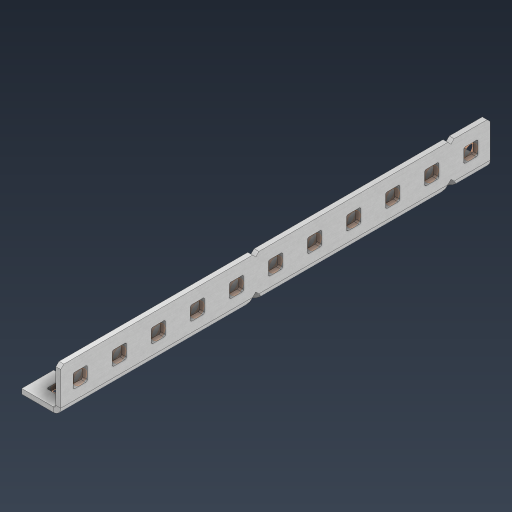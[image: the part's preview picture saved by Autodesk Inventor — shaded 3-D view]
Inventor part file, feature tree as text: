
AUTODESK INVENTOR PART (.ipt)
format: ipt  version: 2024.3 (Build 283343000, 343)  size: 625,664 bytes
history: native  units: in
note: dims shown in document units (in); Inventor stores cm internally (conversion verified against a paired STEP export)
features: other x40, extrude x31, sheet_metal_op x11, pattern_linear x2, mirror x1, chamfer x1, sketch x1
ambient origin geometry x8: Origin, YZ Plane, XZ Plane, XY Plane, X Axis, Y Axis, Z Axis, Center Point
bodies: Solid1 (feature_tree), Body (feature_tree)
feature tree (87):
  sheet_metal_op  "Flanges"
  other  "Flange Pattern Plane"
  other  "Flange Pattern Sketch"
  sheet_metal_op  "Flange Pattern"
  sheet_metal_op  "Body Pattern"
  pattern_linear  "Center Pattern"  Spacing1=5.5in  [1 undecoded]
  other  "Arc Length"
  mirror  "Notch Mirror"
  pattern_linear  "Notch Pattern"  Spacing1=0.0625in  [1 undecoded]
  chamfer  "End Chamfer"
  extrude  "Half Cut"  Depth=0.0625in
  other  "Plate1"
  sketch  "Sketch2"  dims[d0=1.0in d1=5.5in d2=0.0625in d3=0.0625in d4=0.0312in d5=0.125in d6=0.0625in d7=0.5in d8=90.0deg d9=0.0312in d10=0.25in d11=0.0625in d12=0.0625in d16=0.182in d17=0.02in d18=0.0625in d19=0.0in d20=0.25in d21=0.25in d38=4.3307in d40=0.5in d41=0.3937in d43=1.0in d46=0.172in d47=1.0in d48=0.0in d49=0.182in d50=0.02in d51=0.25in d52=0.25in d53=0.0625in d54=0.0in d55=0.172in d56=1.0in d57=0.0in d58=0.25in d60=4.3307in d62=0.5in d63=0.3937in d65=0.5in d85=0.1473in d86=0.1782in d88=0.04in d89=0.0625in d90=0.0in d91=0.04in d92=0.0491in d95=2.5in d96=0.04in d97=0.25in d98=45.0deg d99=0.25in d100=0.5in d101=0.0in d102=2.497in d106=0.182in d107=0.02in d108=0.5in d109=0.5in d110=0.0625in d111=0.0in d112=0.172in d113=0.5in d114=0.0in d117=0.5in d118=0.5in d119=0.5in]
  other  "Plate2"
  sheet_metal_op  "Bend1"
  sheet_metal_op  "Corner1"
  other  "Srf1"
  other  "Srf2"
  other  "Srf91"
  sheet_metal_op  "Body Pattern Sketch"
  other  "Srf92"
  other  "Srf786"
  other  "Srf823"
  other  "Srf824"
  other  "Srf825"
  other  "Srf826"
  other  "Srf827"
  other  "Srf828"
  other  "Srf829"
  other  "Srf856"
  other  "Srf857"
  other  "Srf858"
  other  "Srf859"
  other  "Srf860"
  other  "Srf861"
  other  "Srf862"
  other  "Srf889"
  other  "Srf890"
  other  "Srf891"
  other  "Srf892"
  other  "Srf893"
  other  "Srf894"
  other  "Srf895"
  other  "Srf896"
  other  "Srf922"
  other  "Srf923"
  other  "Srf959"
  other  "Srf960"
  other  "Srf996"
  other  "Srf997"
  sheet_metal_op  "Flange Stamp"
  sheet_metal_op  "Flange Circle"
  sheet_metal_op  "Body Stamp"
  sheet_metal_op  "Body Circle"
  other  "Center Stamp"
  other  "Center Circle"
  sheet_metal_op  "Notch"
  extrude  "ExtrusionSrf2"  Depth=0.0312in
  extrude  "ExtrusionSrf92"  Depth=0.5in
  extrude  "ExtrusionSrf823"  Depth=0.0625in
  extrude  "ExtrusionSrf824"  Depth=0.5in TaperAngle=90.0deg
  extrude  "ExtrusionSrf825"  Depth=0.5in
  extrude  "ExtrusionSrf826"  Depth=0.0625in
  extrude  "ExtrusionSrf827"  Depth=0.0625in
  extrude  "ExtrusionSrf828"  Depth=0.182in
  extrude  "ExtrusionSrf829"  Depth=0.02in
  extrude  "ExtrusionSrf856"  Depth=0.0625in
  extrude  "ExtrusionSrf857"  TaperAngle=0.0deg  [1 undecoded]
  extrude  "ExtrusionSrf858"  Depth=0.5in
  extrude  "ExtrusionSrf859"  Depth=0.5in
  extrude  "ExtrusionSrf860"  Depth=0.5in
  extrude  "ExtrusionSrf861"  Depth=0.5in
  extrude  "ExtrusionSrf862"  Depth=1.0in TaperAngle=0.0deg
  extrude  "ExtrusionSrf889"  Depth=0.182in
  extrude  "ExtrusionSrf890"  Depth=0.02in
  extrude  "ExtrusionSrf891"  Depth=0.5in
  extrude  "ExtrusionSrf892"  Depth=0.5in
  extrude  "ExtrusionSrf893"  Depth=0.0625in
  extrude  "ExtrusionSrf894"  TaperAngle=0.0deg  [1 undecoded]
  extrude  "ExtrusionSrf895"  Depth=0.5in
  extrude  "ExtrusionSrf896"  Depth=1.0in TaperAngle=0.0deg
  extrude  "ExtrusionSrf922"  Depth=0.5in
  extrude  "ExtrusionSrf923"  Depth=0.5in
  extrude  "ExtrusionSrf959"  Depth=0.5in
  extrude  "ExtrusionSrf960"  Depth=0.5in
  extrude  "ExtrusionSrf996"  Depth=0.5in
  extrude  "ExtrusionSrf997"  Depth=0.5in
note: 4 required parameter values undecoded (feature->parameter linkage not recoverable at this tier; creation-order binding heuristic only, values carry confidence <= 0.55)
